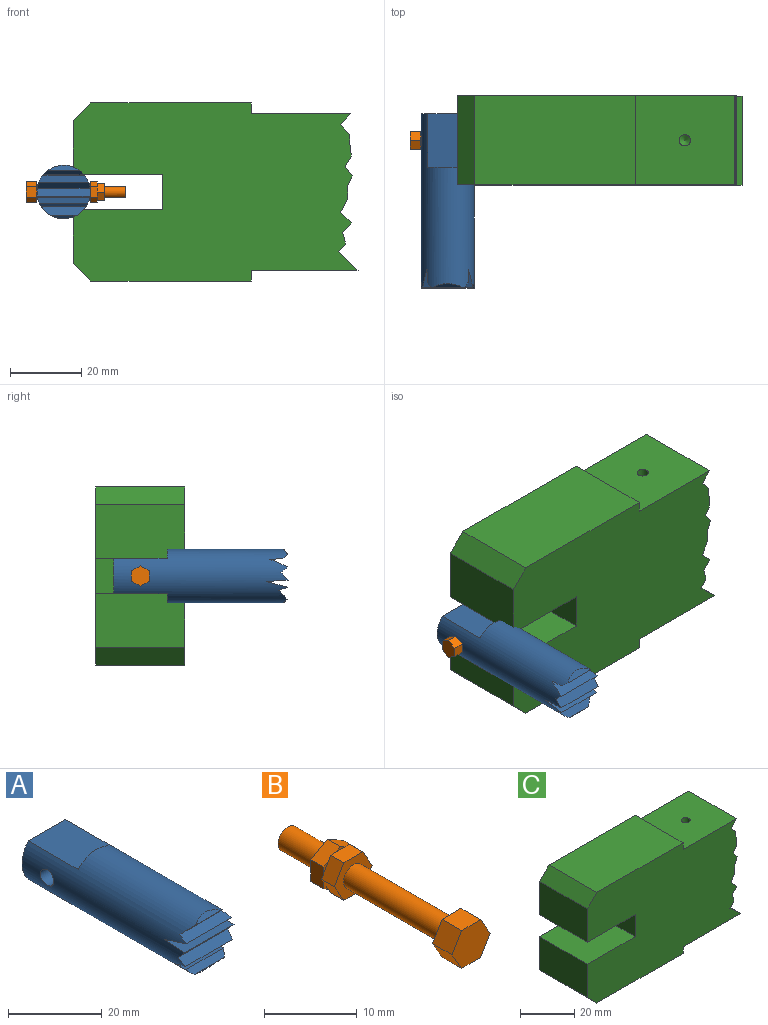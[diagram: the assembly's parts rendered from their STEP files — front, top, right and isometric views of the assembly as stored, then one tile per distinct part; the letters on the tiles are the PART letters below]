
ASSEMBLY  parts=3 mates=3
PART A: 18 faces, bbox 15x49x15 mm
  f0: cylinder r=7.5mm len=49mm, axis (0,1,0), area 1839.5mm2, adj f1,f2,f3,f4,f5,f6,f7,f8
  f1: plane 15x10mm, normal (0,1,0), area 138mm2, adj f0,f14,f16
  f2: plane 9.05x1.52mm, normal (0,-0.78,-0.62), area 12mm2, adj f0,f3
  f3: plane 11.44x1.42mm, normal (0,-0.62,0.78), area 18.7mm2, adj f0,f2,f4
  f4: plane 11.69x3.67mm, normal (0,-0.04,1), area 42.2mm2, adj f0,f3,f5
  f5: plane 14.07x5.03mm, normal (0,-0.39,-0.92), area 71mm2, adj f0,f4,f6
  f6: plane 14.9x1.95mm, normal (0,-0.64,0.77), area 36.5mm2, adj f0,f5,f7
  f7: plane 15x2.15mm, normal (0,-0.73,-0.69), area 44mm2, adj f0,f6,f8
  f8: plane 14.84x6.2mm, normal (0,-0.06,1), area 91.4mm2, adj f0,f7,f9
  f9: plane 14.68x5.95mm, normal (0,-0.26,-0.97), area 87.5mm2, adj f0,f8,f10
  f10: plane 13.62x2.38mm, normal (0,-0.37,0.93), area 33.6mm2, adj f0,f9,f11
  f11: plane 12.57x2.39mm, normal (0,-0.72,-0.69), area 34.7mm2, adj f0,f10,f12
  f12: plane 7.54x1.02mm, normal (0,-0.75,0.66), area 6.9mm2, adj f0,f11
  f13: plane 11.18x2.5mm, normal (0,1,0), area 19.4mm2, adj f0,f14
  f14: plane 15x11.18mm, normal (0,0,1), area 167.7mm2, adj f0,f1,f13
  f15: plane 11.18x2.5mm, normal (0,1,0), area 19.4mm2, adj f0,f16
  f16: plane 15x11.18mm, normal (0,0,-1), area 167.7mm2, adj f0,f1,f15
  f17: cylinder r=2mm len=15mm, axis (1,0,0), area 185.1mm2, adj f0
PART B: 37 faces, bbox 5.8x28x5.8 mm
  f0: plane 1.12x0.65mm, normal (0,1,0), area 0.2mm2, adj f19,f20,f27
  f1: plane 1.12x0.65mm, normal (0,1,0), area 0.2mm2, adj f15,f20,f28
  f2: plane 1.3x0.37mm, normal (0,1,0), area 0.2mm2, adj f15,f16,f29
  f3: plane 1.12x0.65mm, normal (0,1,0), area 0.2mm2, adj f16,f17,f30
  f4: plane 1.12x0.65mm, normal (0,1,0), area 0.2mm2, adj f17,f18,f31
  f5: plane 1.3x0.37mm, normal (0,1,0), area 0.2mm2, adj f18,f19,f32
  f6: plane 3x2.5mm, normal (0.87,0,-0.5), area 8.7mm2, adj f7,f11,f12,f13
  f7: plane 3x2.5mm, normal (0.87,0,0.5), area 8.7mm2, adj f6,f8,f12,f13
  f8: plane 3x2.89mm, normal (0,0,1), area 8.7mm2, adj f7,f9,f12,f13
  f9: plane 3x2.5mm, normal (-0.87,0,0.5), area 8.7mm2, adj f8,f10,f12,f13
  f10: plane 3x2.5mm, normal (-0.87,0,-0.5), area 8.7mm2, adj f9,f11,f12,f13
  f11: plane 3x2.89mm, normal (0,0,-1), area 8.7mm2, adj f6,f10,f12,f13
  f12: plane 5.77x5mm, normal (0,-1,0), area 21.7mm2, adj f6,f7,f8,f9,f10,f11
  f13: plane 5.77x5mm, normal (0,1,0), area 14.6mm2, adj f6,f7,f8,f9,f10,f11,f14
  f14: cylinder r=1.5mm len=15mm, axis (0,-1,0), area 141.4mm2, adj f13,f21
  f15: plane 2.49x2mm, normal (-0.87,0,0.5), area 5.7mm2, adj f1,f2,f16,f20,f21,f22
  f16: plane 2.49x2mm, normal (-0.87,0,-0.5), area 5.7mm2, adj f2,f3,f15,f17,f21,f34
  f17: plane 2.87x2mm, normal (0,0,-1), area 5.7mm2, adj f3,f4,f16,f18,f21,f26
  f18: plane 2.49x2mm, normal (0.87,0,-0.5), area 5.7mm2, adj f4,f5,f17,f19,f21,f25
  f19: plane 2.49x2mm, normal (0.87,0,0.5), area 5.7mm2, adj f0,f5,f18,f20,f21,f24
  f20: plane 2.87x2mm, normal (0,0,1), area 5.7mm2, adj f0,f1,f15,f19,f21,f23
  f21: plane 5.75x4.98mm, normal (0,-1,0), area 14.4mm2, adj f14,f15,f16,f17,f18,f19,f20
  f22: plane 1.19x0.69mm, normal (0,-1,0), area 0.3mm2, adj f15,f28,f29
  f23: plane 1.38x0.4mm, normal (0,-1,0), area 0.3mm2, adj f20,f27,f28
  f24: plane 1.19x0.69mm, normal (0,-1,0), area 0.3mm2, adj f19,f27,f32
  f25: plane 1.19x0.69mm, normal (0,-1,0), area 0.3mm2, adj f18,f31,f32
  f26: plane 1.38x0.4mm, normal (0,-1,0), area 0.3mm2, adj f17,f30,f31
  f27: plane 2.5x2mm, normal (0.5,0,0.87), area 5.8mm2, adj f0,f23,f24,f28,f32,f33
  f28: plane 2.5x2mm, normal (-0.5,0,0.87), area 5.8mm2, adj f1,f22,f23,f27,f29,f33
  f29: plane 2.89x2mm, normal (-1,0,0), area 5.8mm2, adj f2,f22,f28,f30,f33,f34
  f30: plane 2.5x2mm, normal (-0.5,0,-0.87), area 5.8mm2, adj f3,f26,f29,f31,f33,f34
  f31: plane 2.5x2mm, normal (0.5,0,-0.87), area 5.8mm2, adj f4,f25,f26,f30,f32,f33
  f32: plane 2.89x2mm, normal (1,0,0), area 5.8mm2, adj f5,f24,f25,f27,f31,f33
  f33: plane 5.77x5mm, normal (0,1,0), area 14.6mm2, adj f27,f28,f29,f30,f31,f32,f36
  f34: plane 1.19x0.69mm, normal (0,-1,0), area 0.3mm2, adj f16,f29,f30
  f35: plane 3x3mm, normal (0,1,0), area 7.1mm2, adj f36
  f36: cylinder r=1.5mm len=6mm, axis (0,-1,0), area 56.5mm2, adj f33,f35
PART C: 33 faces, bbox 80x25x50 mm
  f0: plane 27.88x25mm, normal (0,0,1), area 688.9mm2, adj f1,f2,f16,f17,f31
  f1: plane 80x50mm, normal (0,-1,0), area 3408.9mm2, adj f0,f3,f4,f5,f6,f7,f8,f9
  f2: plane 80x50mm, normal (0,1,0), area 3408.9mm2, adj f0,f3,f4,f5,f6,f7,f8,f9
  f3: plane 45x25mm, normal (0,0,1), area 1125mm2, adj f1,f2,f8,f16
  f4: plane 45x25mm, normal (0,0,-1), area 1125mm2, adj f1,f2,f7,f15
  f5: plane 25x15mm, normal (-1,0,0), area 375mm2, adj f1,f2,f8,f11
  f6: plane 25x15mm, normal (-1,0,0), area 375mm2, adj f1,f2,f7,f9
  f7: plane 25x5mm, normal (-0.71,0,-0.71), area 176.8mm2, adj f1,f2,f4,f6
  f8: plane 25x5mm, normal (-0.71,0,0.71), area 176.8mm2, adj f1,f2,f3,f5
  f9: plane 25x25mm, normal (0,0,1), area 625mm2, adj f1,f2,f6,f10
  f10: plane 25x10mm, normal (-1,0,0), area 234.8mm2, adj f1,f2,f9,f11,f12
  f11: plane 25x25mm, normal (0,0,-1), area 625mm2, adj f1,f2,f5,f10
  f12: cylinder r=2.2mm len=25mm, axis (-1,0,0), area 345.6mm2, adj f10,f13
  f13: cone r=0mm half-angle=59deg, axis (-1,0,0), area 17.7mm2, adj f12
  f14: plane 30x25mm, normal (0,0,-1), area 750mm2, adj f1,f2,f15,f30
  f15: plane 25x3mm, normal (1,0,0), area 75mm2, adj f1,f2,f4,f14
  f16: plane 25x3mm, normal (1,0,0), area 75mm2, adj f0,f1,f2,f3
  f17: plane 25x3.08mm, normal (0.75,0,-0.66), area 102mm2, adj f0,f1,f2,f18
  f18: plane 25x2.78mm, normal (0.75,0,0.66), area 92.4mm2, adj f1,f2,f17,f19
  f19: plane 25x1.86mm, normal (1,0,0), area 46.5mm2, adj f1,f2,f18,f20
  f20: plane 25x4.18mm, normal (0.99,0,0.11), area 105.1mm2, adj f1,f2,f19,f21
  f21: plane 25x2.86mm, normal (0.85,0,-0.53), area 84.2mm2, adj f1,f2,f20,f22
  f22: plane 25x2.74mm, normal (0.81,0,0.58), area 84.2mm2, adj f1,f2,f21,f23
  f23: plane 25x3.02mm, normal (0.92,0,-0.38), area 81.9mm2, adj f1,f2,f22,f24
  f24: plane 25x3.55mm, normal (1,0,0), area 88.6mm2, adj f1,f2,f23,f25
  f25: plane 25x3.65mm, normal (0.88,0,-0.48), area 104mm2, adj f1,f2,f24,f26
  f26: plane 25x3.05mm, normal (0.7,0,0.71), area 106.7mm2, adj f1,f2,f25,f27
  f27: plane 25x2.62mm, normal (0.73,0,-0.68), area 89.8mm2, adj f1,f2,f26,f28
  f28: plane 25x3.3mm, normal (0.97,0,0.26), area 85.5mm2, adj f1,f2,f27,f29
  f29: plane 25x2.17mm, normal (0.73,0,-0.69), area 74.7mm2, adj f1,f2,f28,f30
  f30: plane 25x5.5mm, normal (0.69,0,0.73), area 189.2mm2, adj f1,f2,f14,f29
  f31: cylinder r=1.6mm len=15mm, axis (0,0,1), area 150.8mm2, adj f0,f32
  f32: cone r=0mm half-angle=59deg, axis (0,0,1), area 9.4mm2, adj f31
PLACE A rot(axis=(0,1,0),180deg) t=(-31.4,-18.22,26.73)mm
PLACE B rot(axis=(-0.58,-0.58,-0.58),120deg) t=(-39,-25.72,26.73)mm
PLACE C t=(11.24,-13.22,26.73)mm
MATE cylindrical B.f14 <-> A.f17  axis (-1,0,0) through (-39,-25.72,26.73)mm
MATE parallel A.f17 <-> C.f12  axis (-1,0,0) through (-39,-25.72,26.73)mm
MATE cylindrical A.f17 <-> C.f12  axis (-1,0,0) through (-39,-25.72,26.73)mm
